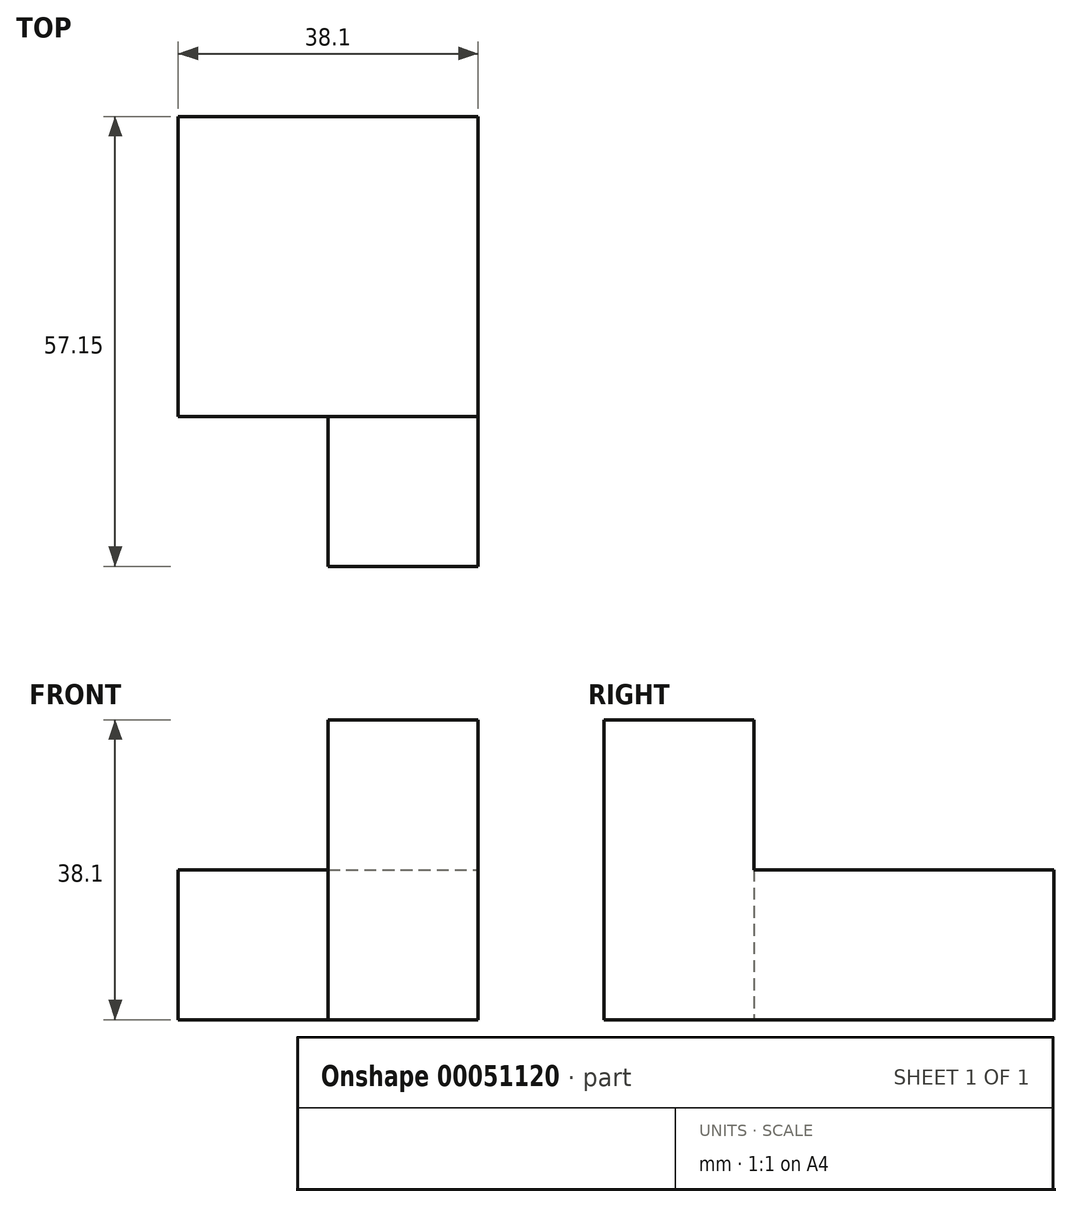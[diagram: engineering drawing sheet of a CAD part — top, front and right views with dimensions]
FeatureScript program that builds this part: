
annotation { "Feature Type Name" : "Feature", "Feature Type Description" : "" }
export const myFeature = defineFeature(function(context is Context, id is Id, definition is map)
    precondition{}
    {
        {
            var Q0;
            Q0=qCreatedBy(makeId("Top.planeOp"),FACE);
            var sketch = newSketch(context, id + "F0", { "sketchPlane" : qUnion([Q0])});
            skLineSegment(sketch, "E0.rect.bottom", {"start": v(-19.05, 19.05) * mm, "end": v(19.05, 19.05) * mm});
            skLineSegment(sketch, "E0.rect.top", {"start": v(-19.05, -19.05) * mm, "end": v(19.05, -19.05) * mm});
            skLineSegment(sketch, "E0.rect.left", {"start": v(-19.05, 19.05) * mm, "end": v(-19.05, -19.05) * mm});
            skLineSegment(sketch, "E0.rect.right", {"start": v(19.05, 19.05) * mm, "end": v(19.05, -19.05) * mm});
            skPoint(sketch, "E0.rect.middle", {"position": v(0, 0) * mm});
            skSolve(sketch);
        }
        {
            var Q0;
            Q0 = qSketchRegion(id + "F0", true);
            extrude(context, id + "F1", {"entities" : qUnion([Q0]), "depth" : 19.05 * mm});
        }
        {
            var Q0;
            Q0=makeQuery(id+"F1.opExtrude","SWEPT_FACE",FACE,{"disambiguationData":[OSD([sQuery(id+"F0.wireOp",EDGE,"E0.rect.top")])]});
            var sketch = newSketch(context, id + "F2", { "sketchPlane" : qUnion([Q0])});
            skLineSegment(sketch, "E1.bottom", {"start": v(19.05, 19.05) * mm, "end": v(0, 19.05) * mm});
            skLineSegment(sketch, "E1.top", {"start": v(19.05, 0) * mm, "end": v(0, 0) * mm});
            skLineSegment(sketch, "E1.left", {"start": v(19.05, 19.05) * mm, "end": v(19.05, 0) * mm});
            skLineSegment(sketch, "E1.right", {"start": v(0, 19.05) * mm, "end": v(0, 0) * mm});
            skSolve(sketch);
        }
        {
            var Q0;
            Q0 = qSketchRegion(id + "F2", true);
            extrude(context, id + "F3", {"entities" : qUnion([Q0]), "operationType" : NewBodyOperationType.ADD, "depth" : 19.05 * mm});
        }
        {
            var Q0;
            Q0=makeQuery(id+"F3.boolean.opBoolean","MERGE",FACE,{"derivedFrom":[makeQuery(id+"F1.opExtrude","CAP_FACE",FACE,{"disambiguationData":[OSD([sQuery(id+"F0.wireOp",EDGE,"E0.rect.bottom"),sQuery(id+"F0.wireOp",EDGE,"E0.rect.top"),sQuery(id+"F0.wireOp",EDGE,"E0.rect.left"),sQuery(id+"F0.wireOp",EDGE,"E0.rect.right")])],"isStart":false}),makeQuery(id+"F3.opExtrude","SWEPT_FACE",FACE,{"disambiguationData":[OSD([sQuery(id+"F2.wireOp",EDGE,"E1.bottom")])]})]});
            var sketch = newSketch(context, id + "F4", { "sketchPlane" : qUnion([Q0])});
            skLineSegment(sketch, "E2.bottom", {"start": v(0, -19.05) * mm, "end": v(19.05, -19.05) * mm});
            skLineSegment(sketch, "E2.top", {"start": v(0, -38.1) * mm, "end": v(19.05, -38.1) * mm});
            skLineSegment(sketch, "E2.left", {"start": v(0, -19.05) * mm, "end": v(0, -38.1) * mm});
            skLineSegment(sketch, "E2.right", {"start": v(19.05, -19.05) * mm, "end": v(19.05, -38.1) * mm});
            skSolve(sketch);
        }
        {
            var Q0;
            Q0 = qSketchRegion(id + "F4", true);
            extrude(context, id + "F5", {"entities" : qUnion([Q0]), "operationType" : NewBodyOperationType.ADD, "depth" : 19.05 * mm});
        }
    });
